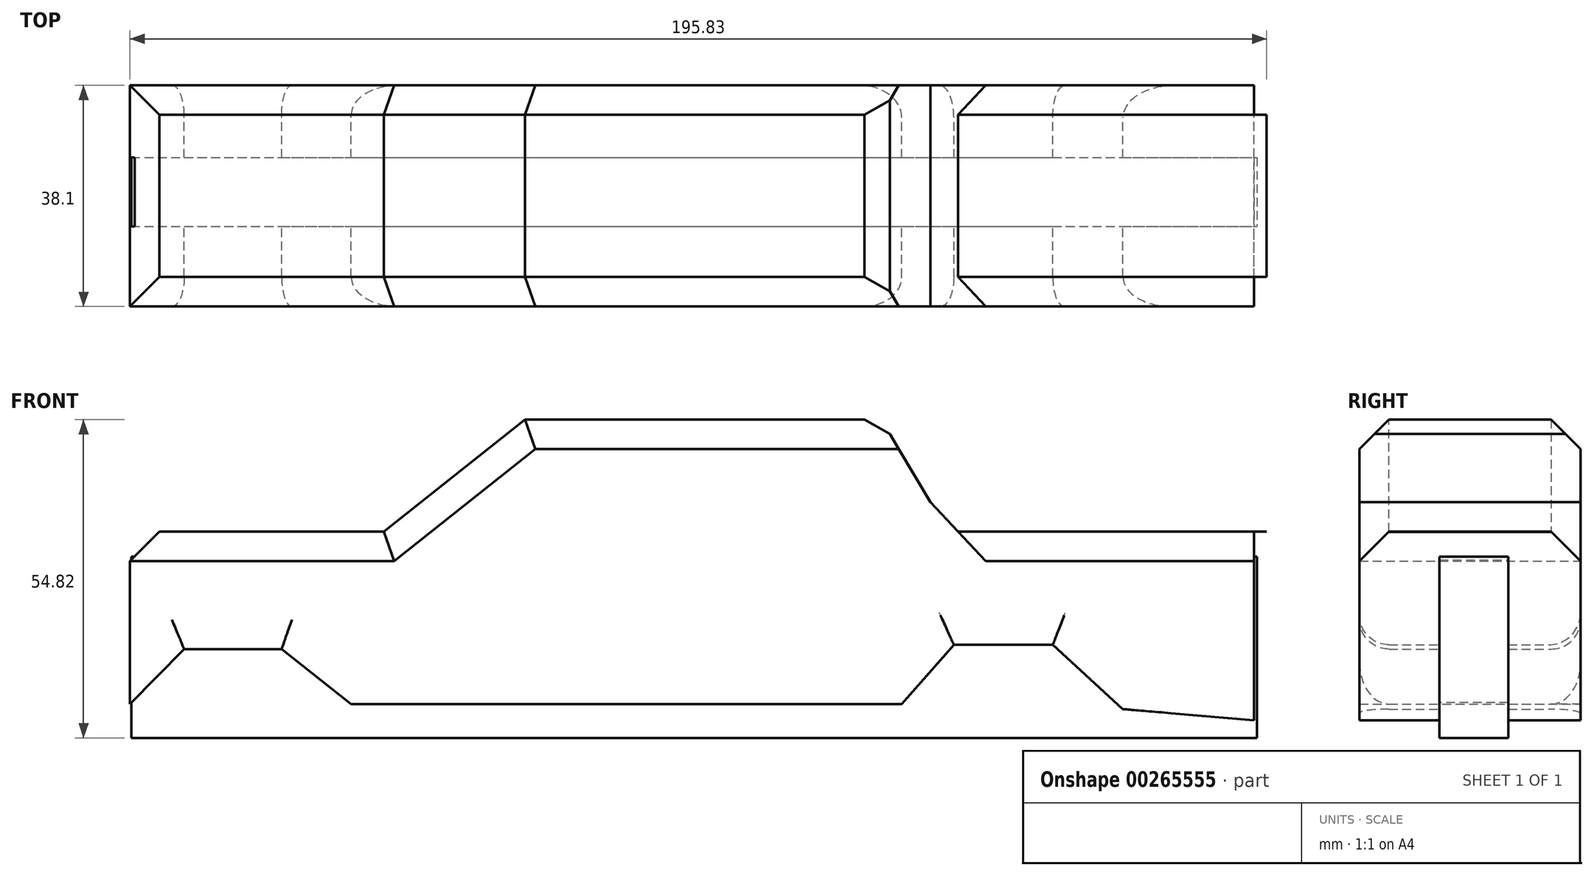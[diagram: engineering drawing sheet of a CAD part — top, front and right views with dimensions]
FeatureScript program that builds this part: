
annotation { "Feature Type Name" : "Feature", "Feature Type Description" : "" }
export const myFeature = defineFeature(function(context is Context, id is Id, definition is map)
    precondition{}
    {
        {
            var Q0;
            Q0=qCreatedBy(makeId("Front.planeOp"),FACE);
            var sketch = newSketch(context, id + "F0", { "sketchPlane" : qUnion([Q0])});
            skLineSegment(sketch, "E0", {"start": v(90.9, -32.48) * mm, "end": v(90.9, -19.55) * mm});
            skLineSegment(sketch, "E1", {"start": v(90.9, -19.55) * mm, "end": v(90.9, -0.05) * mm});
            skLineSegment(sketch, "E2", {"start": v(90.9, -0.05) * mm, "end": v(93.07, 0) * mm});
            skLineSegment(sketch, "E3", {"start": v(93.07, 0) * mm, "end": v(60.8, 0) * mm});
            skLineSegment(sketch, "E4", {"start": v(60.8, 0) * mm, "end": v(39.92, 0) * mm});
            skLineSegment(sketch, "E5", {"start": v(39.92, 0) * mm, "end": v(35.14, 5.1) * mm});
            skLineSegment(sketch, "E6", {"start": v(35.14, 5.1) * mm, "end": v(26.69, 19.29) * mm});
            skLineSegment(sketch, "E7", {"start": v(26.69, 19.29) * mm, "end": v(6.68, 19.29) * mm});
            skLineSegment(sketch, "E8", {"start": v(6.68, 19.29) * mm, "end": v(-19.68, 19.29) * mm});
            skLineSegment(sketch, "E9", {"start": v(-19.68, 19.29) * mm, "end": v(-34.7, 19.29) * mm});
            skLineSegment(sketch, "E10", {"start": v(-34.7, 19.29) * mm, "end": v(-59.03, 0) * mm});
            skLineSegment(sketch, "E11", {"start": v(-59.03, 0) * mm, "end": v(-76.25, 0) * mm});
            skLineSegment(sketch, "E12", {"start": v(-76.25, 0) * mm, "end": v(-85.74, 0) * mm});
            skLineSegment(sketch, "E13", {"start": v(-85.74, 0) * mm, "end": v(-102.76, 0) * mm});
            skLineSegment(sketch, "E14", {"start": v(-102.76, 0) * mm, "end": v(-102.76, -29.7) * mm});
            skLineSegment(sketch, "E15", {"start": v(-102.76, -29.7) * mm, "end": v(-93.43, -20.24) * mm});
            skLineSegment(sketch, "E16", {"start": v(-93.43, -20.24) * mm, "end": v(-86.8, -20.24) * mm});
            skLineSegment(sketch, "E17", {"start": v(-86.8, -20.24) * mm, "end": v(-78.71, -20.24) * mm});
            skLineSegment(sketch, "E18", {"start": v(-78.71, -20.24) * mm, "end": v(-76.63, -20.24) * mm});
            skLineSegment(sketch, "E19", {"start": v(-76.63, -20.24) * mm, "end": v(-64.66, -29.7) * mm});
            skLineSegment(sketch, "E20", {"start": v(-64.66, -29.7) * mm, "end": v(-40.76, -29.7) * mm});
            skLineSegment(sketch, "E21", {"start": v(-40.76, -29.7) * mm, "end": v(-19.68, -29.7) * mm});
            skLineSegment(sketch, "E22", {"start": v(-19.68, -29.7) * mm, "end": v(0, -29.7) * mm});
            skLineSegment(sketch, "E23", {"start": v(0, -29.7) * mm, "end": v(14.06, -29.7) * mm});
            skLineSegment(sketch, "E24", {"start": v(14.06, -29.7) * mm, "end": v(30.22, -29.7) * mm});
            skLineSegment(sketch, "E25", {"start": v(30.22, -29.7) * mm, "end": v(39.18, -19.5) * mm});
            skLineSegment(sketch, "E26", {"start": v(39.18, -19.5) * mm, "end": v(56.22, -19.5) * mm});
            skLineSegment(sketch, "E27", {"start": v(56.22, -19.5) * mm, "end": v(68.32, -30.57) * mm});
            skLineSegment(sketch, "E28", {"start": v(68.32, -30.57) * mm, "end": v(90.9, -32.48) * mm});
            skSolve(sketch);
        }
        {
            var Q0;
            Q0=makeQuery(id+"F0.imprint","IMPRINT",FACE,{"disambiguationData":[TD([[makeQuery(id+"F0.imprint","IMPRINT",EDGE,{"derivedFrom":sQuery(id+"F0.wireOp",EDGE,"E0")}),1.0]])]});
            extrude(context, id + "F1", {"entities" : qUnion([Q0]), "depth" : 38.1 * mm});
        }
        {
            var Q0;
            Q0=makeQuery(id+"F1.opExtrude","CAP_EDGE",EDGE,{"disambiguationData":[OSD([sQuery(id+"F0.wireOp",EDGE,"E11"),sQuery(id+"F0.wireOp",EDGE,"E12"),sQuery(id+"F0.wireOp",EDGE,"E13")])],"isStart":false});
            var Q1;
            Q1=makeQuery(id+"F1.opExtrude","SWEPT_EDGE",EDGE,{"disambiguationData":[OSD([sQuery(id+"F0.wireOp",EDGE,"E13"),sQuery(id+"F0.wireOp",EDGE,"E14")])]});
            var Q2;
            Q2=makeQuery(id+"F1.opExtrude","CAP_EDGE",EDGE,{"disambiguationData":[OSD([sQuery(id+"F0.wireOp",EDGE,"E11"),sQuery(id+"F0.wireOp",EDGE,"E12"),sQuery(id+"F0.wireOp",EDGE,"E13")])],"isStart":true});
            var Q3;
            Q3=makeQuery(id+"F1.opExtrude","CAP_EDGE",EDGE,{"disambiguationData":[OSD([sQuery(id+"F0.wireOp",EDGE,"E10")])],"isStart":false});
            var Q4;
            Q4=makeQuery(id+"F1.opExtrude","CAP_EDGE",EDGE,{"disambiguationData":[OSD([sQuery(id+"F0.wireOp",EDGE,"E10")])],"isStart":true});
            var Q5;
            Q5=makeQuery(id+"F1.opExtrude","SWEPT_EDGE",EDGE,{"disambiguationData":[OSD([sQuery(id+"F0.wireOp",EDGE,"E6"),sQuery(id+"F0.wireOp",EDGE,"E7")])]});
            chamfer(context, id + "F2", {"entities" : qUnion([Q0, Q1, Q2, Q3, Q4, Q5]), "width" : 5.08 * mm, "tangentPropagation" : true});
        }
        {
            var Q0;
            Q0=makeQuery(id+"F1.opExtrude","CAP_EDGE",EDGE,{"disambiguationData":[OSD([sQuery(id+"F0.wireOp",EDGE,"E27")])],"isStart":true});
            var Q1;
            Q1=makeQuery(id+"F1.opExtrude","CAP_EDGE",EDGE,{"disambiguationData":[OSD([sQuery(id+"F0.wireOp",EDGE,"E26")])],"isStart":true});
            var Q2;
            Q2=makeQuery(id+"F1.opExtrude","CAP_EDGE",EDGE,{"disambiguationData":[OSD([sQuery(id+"F0.wireOp",EDGE,"E25")])],"isStart":true});
            fillet(context, id + "F3", {"entities" : qUnion([Q0, Q1, Q2]), "radius" : 5.52 * mm, "tangentPropagation" : true, "allowEdgeOverflow" : false});
        }
        {
            var Q0;
            Q0=makeQuery(id+"F1.opExtrude","CAP_EDGE",EDGE,{"disambiguationData":[OSD([sQuery(id+"F0.wireOp",EDGE,"E25")])],"isStart":false});
            var Q1;
            Q1=makeQuery(id+"F1.opExtrude","CAP_EDGE",EDGE,{"disambiguationData":[OSD([sQuery(id+"F0.wireOp",EDGE,"E26")])],"isStart":false});
            var Q2;
            Q2=makeQuery(id+"F1.opExtrude","CAP_EDGE",EDGE,{"disambiguationData":[OSD([sQuery(id+"F0.wireOp",EDGE,"E27")])],"isStart":false});
            var Q3;
            Q3=makeQuery(id+"F1.opExtrude","CAP_EDGE",EDGE,{"disambiguationData":[OSD([sQuery(id+"F0.wireOp",EDGE,"E19")])],"isStart":true});
            var Q4;
            Q4=makeQuery(id+"F1.opExtrude","CAP_EDGE",EDGE,{"disambiguationData":[OSD([sQuery(id+"F0.wireOp",EDGE,"E16"),sQuery(id+"F0.wireOp",EDGE,"E17"),sQuery(id+"F0.wireOp",EDGE,"E18")])],"isStart":true});
            var Q5;
            Q5=makeQuery(id+"F1.opExtrude","CAP_EDGE",EDGE,{"disambiguationData":[OSD([sQuery(id+"F0.wireOp",EDGE,"E15")])],"isStart":true});
            var Q6;
            Q6=makeQuery(id+"F1.opExtrude","CAP_EDGE",EDGE,{"disambiguationData":[OSD([sQuery(id+"F0.wireOp",EDGE,"E16"),sQuery(id+"F0.wireOp",EDGE,"E17"),sQuery(id+"F0.wireOp",EDGE,"E18")])],"isStart":false});
            var Q7;
            Q7=makeQuery(id+"F1.opExtrude","CAP_EDGE",EDGE,{"disambiguationData":[OSD([sQuery(id+"F0.wireOp",EDGE,"E19")])],"isStart":false});
            var Q8;
            Q8=makeQuery(id+"F1.opExtrude","CAP_EDGE",EDGE,{"disambiguationData":[OSD([sQuery(id+"F0.wireOp",EDGE,"E15")])],"isStart":false});
            fillet(context, id + "F4", {"entities" : qUnion([Q0, Q1, Q2, Q3, Q4, Q5, Q6, Q7, Q8]), "radius" : 5.08 * mm, "tangentPropagation" : true, "allowEdgeOverflow" : false});
        }
        {
            var Q0;
            Q0=makeQuery(id+"F1.opExtrude","CAP_EDGE",EDGE,{"disambiguationData":[OSD([sQuery(id+"F0.wireOp",EDGE,"E3"),sQuery(id+"F0.wireOp",EDGE,"E4")])],"isStart":false});
            var Q1;
            Q1=makeQuery(id+"F1.opExtrude","CAP_EDGE",EDGE,{"disambiguationData":[OSD([sQuery(id+"F0.wireOp",EDGE,"E3"),sQuery(id+"F0.wireOp",EDGE,"E4")])],"isStart":true});
            chamfer(context, id + "F5", {"entities" : qUnion([Q0, Q1]), "width" : 5.08 * mm, "tangentPropagation" : true});
        }
        {
            var Q0;
            Q0=makeQuery(id+"F1.opExtrude","CAP_EDGE",EDGE,{"disambiguationData":[OSD([sQuery(id+"F0.wireOp",EDGE,"E7"),sQuery(id+"F0.wireOp",EDGE,"E8"),sQuery(id+"F0.wireOp",EDGE,"E9")])],"isStart":true});
            var Q1;
            Q1=makeQuery(id+"F1.opExtrude","CAP_EDGE",EDGE,{"disambiguationData":[OSD([sQuery(id+"F0.wireOp",EDGE,"E7"),sQuery(id+"F0.wireOp",EDGE,"E8"),sQuery(id+"F0.wireOp",EDGE,"E9")])],"isStart":false});
            chamfer(context, id + "F6", {"entities" : qUnion([Q0, Q1]), "width" : 5.08 * mm, "tangentPropagation" : true});
        }
        {
            var Q0;
            Q0=makeQuery(id+"F1.opExtrude","SWEPT_FACE",FACE,{"disambiguationData":[OSD([sQuery(id+"F0.wireOp",EDGE,"E20"),sQuery(id+"F0.wireOp",EDGE,"E21"),sQuery(id+"F0.wireOp",EDGE,"E22"),sQuery(id+"F0.wireOp",EDGE,"E23"),sQuery(id+"F0.wireOp",EDGE,"E24")])]});
            var sketch = newSketch(context, id + "F7", { "sketchPlane" : qUnion([Q0])});
            skLineSegment(sketch, "E29.right", {"start": v(90.12, 23.5) * mm, "end": v(90.12, 0) * mm});
            skLineSegment(sketch, "E30.bottom", {"start": v(-102.53, 12.45) * mm, "end": v(91.41, 12.45) * mm});
            skLineSegment(sketch, "E30.top", {"start": v(-102.53, 24.32) * mm, "end": v(91.41, 24.32) * mm});
            skLineSegment(sketch, "E30.left", {"start": v(-102.53, 12.45) * mm, "end": v(-102.53, 24.32) * mm});
            skLineSegment(sketch, "E30.right", {"start": v(91.41, 12.45) * mm, "end": v(91.41, 24.32) * mm});
            skSolve(sketch);
        }
        {
            var Q0;
            Q0 = qSketchRegion(id + "F7", true);
            extrude(context, id + "F8", {"entities" : qUnion([Q0]), "operationType" : NewBodyOperationType.ADD, "depth" : 5.84 * mm, "hasSecondDirection" : true, "secondDirectionOppositeDirection" : true, "secondDirectionDepth" : 25.4 * mm});
        }
    });
